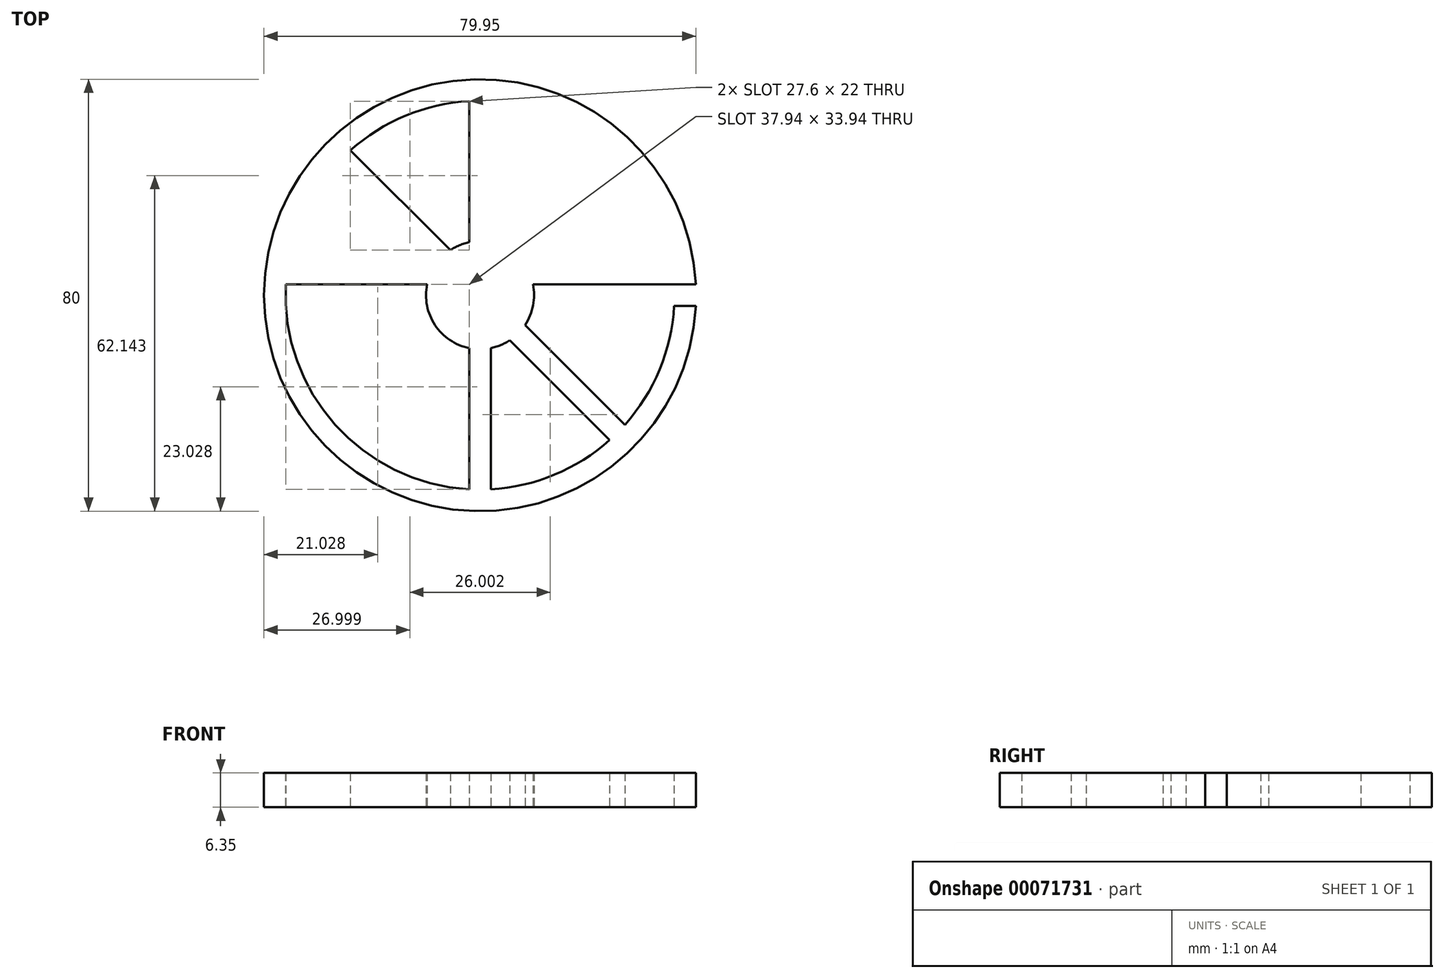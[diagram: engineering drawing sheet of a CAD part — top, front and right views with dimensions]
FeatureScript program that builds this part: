
annotation { "Feature Type Name" : "Feature", "Feature Type Description" : "" }
export const myFeature = defineFeature(function(context is Context, id is Id, definition is map)
    precondition{}
    {
        {
            var Q0;
            Q0=qCreatedBy(makeId("Top.planeOp"),FACE);
            var sketch = newSketch(context, id + "F0", { "sketchPlane" : qUnion([Q0])});
            skCircle(sketch, "E0", {"center": v(0, 0) * mm, "radius": 40 * mm});
            skCircle(sketch, "E1", {"center": v(0, 0) * mm, "radius": 36 * mm});
            skLineSegment(sketch, "E2.bottom", {"start": v(-2, 40) * mm, "end": v(2, 40) * mm});
            skLineSegment(sketch, "E2.top", {"start": v(-2, -40) * mm, "end": v(2, -40) * mm});
            skLineSegment(sketch, "E2.left", {"start": v(-2, 40) * mm, "end": v(-2, -40) * mm});
            skLineSegment(sketch, "E2.right", {"start": v(2, 40) * mm, "end": v(2, -40) * mm});
            skLineSegment(sketch, "E3", {"start": v(2, 0) * mm, "end": v(-2, 0) * mm, "construction": true});
            skPoint(sketch, "E3.endSnap0", {"position": v(-2, 0) * mm});
            skLineSegment(sketch, "E4.bottom", {"start": v(-40, -2) * mm, "end": v(40, -2) * mm});
            skLineSegment(sketch, "E4.top", {"start": v(-40, 2) * mm, "end": v(40, 2) * mm});
            skLineSegment(sketch, "E4.left", {"start": v(-40, 2) * mm, "end": v(-40, -2) * mm});
            skLineSegment(sketch, "E4.right", {"start": v(40, 2) * mm, "end": v(40, -2) * mm});
            skLineSegment(sketch, "E5", {"start": v(0, 2) * mm, "end": v(0, -2) * mm, "construction": true});
            skLineSegment(sketch, "E6.bottom", {"start": v(-26.87, -29.7) * mm, "end": v(29.7, 26.87) * mm});
            skLineSegment(sketch, "E6.top", {"start": v(-29.7, -26.87) * mm, "end": v(26.87, 29.7) * mm});
            skLineSegment(sketch, "E6.left", {"start": v(-29.7, -26.87) * mm, "end": v(-26.87, -29.7) * mm});
            skLineSegment(sketch, "E6.right", {"start": v(26.87, 29.7) * mm, "end": v(29.7, 26.87) * mm});
            skLineSegment(sketch, "E7", {"start": v(-1.41, 1.41) * mm, "end": v(1.41, -1.41) * mm, "construction": true});
            skLineSegment(sketch, "E8.bottom", {"start": v(-29.7, 26.87) * mm, "end": v(-26.87, 29.7) * mm});
            skLineSegment(sketch, "E8.top", {"start": v(26.87, -29.7) * mm, "end": v(29.7, -26.87) * mm});
            skLineSegment(sketch, "E8.left", {"start": v(-29.7, 26.87) * mm, "end": v(26.87, -29.7) * mm});
            skLineSegment(sketch, "E8.right", {"start": v(-26.87, 29.7) * mm, "end": v(29.7, -26.87) * mm});
            skLineSegment(sketch, "E9", {"start": v(-1.41, -1.41) * mm, "end": v(1.41, 1.41) * mm, "construction": true});
            skCircle(sketch, "E10", {"center": v(0, 0) * mm, "radius": 10 * mm});
            skSolve(sketch);
        }
        {
            var Q0;
            {var subQ0=sQuery(id+"F0.wireOp",EDGE,"E2.left");var subQ1=sQuery(id+"F0.wireOp",EDGE,"E0");var subQ2=makeQuery(id+"F0.imprint","INTERSECT",VERTEX,{"disambiguationData":[OD(0.0)],"derivedFrom":[subQ1,subQ0]});Q0=makeQuery(id+"F0.imprint","IMPRINT",FACE,{"disambiguationData":[TD([[makeQuery(id+"F0.imprint","IMPRINT",EDGE,{"disambiguationData":[TD([[subQ2,-1.0]])],"derivedFrom":subQ1}),1.0]])]});}
            var Q1;
            {var subQ1=sQuery(id+"F0.wireOp",EDGE,"E0");var subQ5=sQuery(id+"F0.wireOp",EDGE,"E2.right");var subQ7=makeQuery(id+"F0.imprint","INTERSECT",VERTEX,{"disambiguationData":[OD(0.0)],"derivedFrom":[subQ1,subQ5]});Q1=makeQuery(id+"F0.imprint","IMPRINT",FACE,{"disambiguationData":[TD([[makeQuery(id+"F0.imprint","IMPRINT",EDGE,{"disambiguationData":[TD([[subQ7,-1.0]])],"derivedFrom":subQ1}),1.0]])]});}
            var Q2;
            {var subQ0=sQuery(id+"F0.wireOp",EDGE,"E6.top");var subQ1=sQuery(id+"F0.wireOp",EDGE,"E0");var subQ2=makeQuery(id+"F0.imprint","INTERSECT",VERTEX,{"disambiguationData":[OD(0.0)],"derivedFrom":[subQ1,subQ0]});Q2=makeQuery(id+"F0.imprint","IMPRINT",FACE,{"disambiguationData":[TD([[makeQuery(id+"F0.imprint","IMPRINT",EDGE,{"disambiguationData":[TD([[subQ2,-1.0]])],"derivedFrom":subQ1}),1.0]])]});}
            var Q3;
            {var subQ0=sQuery(id+"F0.wireOp",EDGE,"E6.bottom");var subQ1=sQuery(id+"F0.wireOp",EDGE,"E0");var subQ2=makeQuery(id+"F0.imprint","INTERSECT",VERTEX,{"disambiguationData":[OD(0.0)],"derivedFrom":[subQ1,subQ0]});Q3=makeQuery(id+"F0.imprint","IMPRINT",FACE,{"disambiguationData":[TD([[makeQuery(id+"F0.imprint","IMPRINT",EDGE,{"disambiguationData":[TD([[subQ2,-1.0]])],"derivedFrom":subQ1}),1.0]])]});}
            var Q4;
            {var subQ0=sQuery(id+"F0.wireOp",EDGE,"E4.top");var subQ1=sQuery(id+"F0.wireOp",EDGE,"E0");var subQ2=makeQuery(id+"F0.imprint","INTERSECT",VERTEX,{"disambiguationData":[OD(0.0)],"derivedFrom":[subQ1,subQ0]});Q4=makeQuery(id+"F0.imprint","IMPRINT",FACE,{"disambiguationData":[TD([[makeQuery(id+"F0.imprint","IMPRINT",EDGE,{"disambiguationData":[TD([[subQ2,-1.0]])],"derivedFrom":subQ1}),1.0]])]});}
            var Q5;
            {var subQ1=sQuery(id+"F0.wireOp",EDGE,"E0");var subQ5=sQuery(id+"F0.wireOp",EDGE,"E4.top");var subQ7=makeQuery(id+"F0.imprint","INTERSECT",VERTEX,{"disambiguationData":[OD(0.0)],"derivedFrom":[subQ1,subQ5]});Q5=makeQuery(id+"F0.imprint","IMPRINT",FACE,{"disambiguationData":[TD([[makeQuery(id+"F0.imprint","IMPRINT",EDGE,{"disambiguationData":[TD([[subQ7,1.0]])],"derivedFrom":subQ1}),1.0]])]});}
            var Q6;
            {var subQ0=sQuery(id+"F0.wireOp",EDGE,"E8.right");var subQ1=sQuery(id+"F0.wireOp",EDGE,"E0");var subQ2=makeQuery(id+"F0.imprint","INTERSECT",VERTEX,{"disambiguationData":[OD(1.0)],"derivedFrom":[subQ1,subQ0]});Q6=makeQuery(id+"F0.imprint","IMPRINT",FACE,{"disambiguationData":[TD([[makeQuery(id+"F0.imprint","IMPRINT",EDGE,{"disambiguationData":[TD([[subQ2,-1.0]])],"derivedFrom":subQ1}),1.0]])]});}
            var Q7;
            {var subQ0=sQuery(id+"F0.wireOp",EDGE,"E8.left");var subQ1=sQuery(id+"F0.wireOp",EDGE,"E0");var subQ2=makeQuery(id+"F0.imprint","INTERSECT",VERTEX,{"disambiguationData":[OD(1.0)],"derivedFrom":[subQ1,subQ0]});Q7=makeQuery(id+"F0.imprint","IMPRINT",FACE,{"disambiguationData":[TD([[makeQuery(id+"F0.imprint","IMPRINT",EDGE,{"disambiguationData":[TD([[subQ2,-1.0]])],"derivedFrom":subQ1}),1.0]])]});}
            var Q8;
            {var subQ0=sQuery(id+"F0.wireOp",EDGE,"E2.right");var subQ1=sQuery(id+"F0.wireOp",EDGE,"E0");var subQ2=makeQuery(id+"F0.imprint","INTERSECT",VERTEX,{"disambiguationData":[OD(1.0)],"derivedFrom":[subQ1,subQ0]});Q8=makeQuery(id+"F0.imprint","IMPRINT",FACE,{"disambiguationData":[TD([[makeQuery(id+"F0.imprint","IMPRINT",EDGE,{"disambiguationData":[TD([[subQ2,-1.0]])],"derivedFrom":subQ1}),1.0]])]});}
            var Q9;
            {var subQ0=sQuery(id+"F0.wireOp",EDGE,"E2.left");var subQ5=sQuery(id+"F0.wireOp",EDGE,"E0");var subQ6=makeQuery(id+"F0.imprint","INTERSECT",VERTEX,{"disambiguationData":[OD(1.0)],"derivedFrom":[subQ5,subQ0]});Q9=makeQuery(id+"F0.imprint","IMPRINT",FACE,{"disambiguationData":[TD([[makeQuery(id+"F0.imprint","IMPRINT",EDGE,{"disambiguationData":[TD([[subQ6,-1.0]])],"derivedFrom":subQ5}),1.0]])]});}
            var Q10;
            {var subQ0=sQuery(id+"F0.wireOp",EDGE,"E6.bottom");var subQ1=sQuery(id+"F0.wireOp",EDGE,"E0");var subQ2=makeQuery(id+"F0.imprint","INTERSECT",VERTEX,{"disambiguationData":[OD(1.0)],"derivedFrom":[subQ1,subQ0]});Q10=makeQuery(id+"F0.imprint","IMPRINT",FACE,{"disambiguationData":[TD([[makeQuery(id+"F0.imprint","IMPRINT",EDGE,{"disambiguationData":[TD([[subQ2,-1.0]])],"derivedFrom":subQ1}),1.0]])]});}
            var Q11;
            {var subQ1=sQuery(id+"F0.wireOp",EDGE,"E0");var subQ5=sQuery(id+"F0.wireOp",EDGE,"E6.top");var subQ6=makeQuery(id+"F0.imprint","INTERSECT",VERTEX,{"disambiguationData":[OD(1.0)],"derivedFrom":[subQ1,subQ5]});Q11=makeQuery(id+"F0.imprint","IMPRINT",FACE,{"disambiguationData":[TD([[makeQuery(id+"F0.imprint","IMPRINT",EDGE,{"disambiguationData":[TD([[subQ6,-1.0]])],"derivedFrom":subQ1}),1.0]])]});}
            var Q12;
            {var subQ0=sQuery(id+"F0.wireOp",EDGE,"E4.bottom");var subQ1=sQuery(id+"F0.wireOp",EDGE,"E0");var subQ2=makeQuery(id+"F0.imprint","INTERSECT",VERTEX,{"disambiguationData":[OD(0.0)],"derivedFrom":[subQ1,subQ0]});Q12=makeQuery(id+"F0.imprint","IMPRINT",FACE,{"disambiguationData":[TD([[makeQuery(id+"F0.imprint","IMPRINT",EDGE,{"disambiguationData":[TD([[subQ2,-1.0]])],"derivedFrom":subQ1}),1.0]])]});}
            var Q13;
            {var subQ1=sQuery(id+"F0.wireOp",EDGE,"E0");var subQ5=sQuery(id+"F0.wireOp",EDGE,"E4.top");var subQ8=makeQuery(id+"F0.imprint","INTERSECT",VERTEX,{"disambiguationData":[OD(1.0)],"derivedFrom":[subQ1,subQ5]});Q13=makeQuery(id+"F0.imprint","IMPRINT",FACE,{"disambiguationData":[TD([[makeQuery(id+"F0.imprint","IMPRINT",EDGE,{"disambiguationData":[TD([[subQ8,-1.0]])],"derivedFrom":subQ1}),1.0]])]});}
            var Q14;
            {var subQ0=sQuery(id+"F0.wireOp",EDGE,"E8.left");var subQ1=sQuery(id+"F0.wireOp",EDGE,"E0");var subQ2=makeQuery(id+"F0.imprint","INTERSECT",VERTEX,{"disambiguationData":[OD(0.0)],"derivedFrom":[subQ1,subQ0]});Q14=makeQuery(id+"F0.imprint","IMPRINT",FACE,{"disambiguationData":[TD([[makeQuery(id+"F0.imprint","IMPRINT",EDGE,{"disambiguationData":[TD([[subQ2,-1.0]])],"derivedFrom":subQ1}),1.0]])]});}
            var Q15;
            {var subQ1=sQuery(id+"F0.wireOp",EDGE,"E0");var subQ5=sQuery(id+"F0.wireOp",EDGE,"E8.right");var subQ6=makeQuery(id+"F0.imprint","INTERSECT",VERTEX,{"disambiguationData":[OD(0.0)],"derivedFrom":[subQ1,subQ5]});Q15=makeQuery(id+"F0.imprint","IMPRINT",FACE,{"disambiguationData":[TD([[makeQuery(id+"F0.imprint","IMPRINT",EDGE,{"disambiguationData":[TD([[subQ6,-1.0]])],"derivedFrom":subQ1}),1.0]])]});}
            var Q16;
            {var subQ0=sQuery(id+"F0.wireOp",EDGE,"E2.right");var subQ1=sQuery(id+"F0.wireOp",EDGE,"E1");var subQ2=makeQuery(id+"F0.imprint","INTERSECT",VERTEX,{"disambiguationData":[OD(0.0)],"derivedFrom":[subQ1,subQ0]});Q16=makeQuery(id+"F0.imprint","IMPRINT",FACE,{"disambiguationData":[TD([[makeQuery(id+"F0.imprint","IMPRINT",EDGE,{"disambiguationData":[TD([[subQ2,-1.0]])],"derivedFrom":subQ1}),1.0]])]});}
            var Q17;
            {var subQ0=sQuery(id+"F0.wireOp",EDGE,"E6.bottom");var subQ1=sQuery(id+"F0.wireOp",EDGE,"E1");var subQ2=makeQuery(id+"F0.imprint","INTERSECT",VERTEX,{"disambiguationData":[OD(0.0)],"derivedFrom":[subQ1,subQ0]});Q17=makeQuery(id+"F0.imprint","IMPRINT",FACE,{"disambiguationData":[TD([[makeQuery(id+"F0.imprint","IMPRINT",EDGE,{"disambiguationData":[TD([[subQ2,-1.0]])],"derivedFrom":subQ1}),1.0]])]});}
            var Q18;
            {var subQ0=sQuery(id+"F0.wireOp",EDGE,"E4.top");var subQ1=sQuery(id+"F0.wireOp",EDGE,"E1");var subQ2=makeQuery(id+"F0.imprint","INTERSECT",VERTEX,{"disambiguationData":[OD(0.0)],"derivedFrom":[subQ1,subQ0]});Q18=makeQuery(id+"F0.imprint","IMPRINT",FACE,{"disambiguationData":[TD([[makeQuery(id+"F0.imprint","IMPRINT",EDGE,{"disambiguationData":[TD([[subQ2,1.0]])],"derivedFrom":subQ1}),1.0]])]});}
            var Q19;
            {var subQ0=sQuery(id+"F0.wireOp",EDGE,"E8.right");var subQ1=sQuery(id+"F0.wireOp",EDGE,"E1");var subQ2=makeQuery(id+"F0.imprint","INTERSECT",VERTEX,{"disambiguationData":[OD(0.0)],"derivedFrom":[subQ1,subQ0]});Q19=makeQuery(id+"F0.imprint","IMPRINT",FACE,{"disambiguationData":[TD([[makeQuery(id+"F0.imprint","IMPRINT",EDGE,{"disambiguationData":[TD([[subQ2,-1.0]])],"derivedFrom":subQ1}),1.0]])]});}
            var Q20;
            {var subQ0=sQuery(id+"F0.wireOp",EDGE,"E4.top");var subQ1=sQuery(id+"F0.wireOp",EDGE,"E1");var subQ2=makeQuery(id+"F0.imprint","INTERSECT",VERTEX,{"disambiguationData":[OD(1.0)],"derivedFrom":[subQ1,subQ0]});Q20=makeQuery(id+"F0.imprint","IMPRINT",FACE,{"disambiguationData":[TD([[makeQuery(id+"F0.imprint","IMPRINT",EDGE,{"disambiguationData":[TD([[subQ2,-1.0]])],"derivedFrom":subQ1}),1.0]])]});}
            var Q21;
            {var subQ0=sQuery(id+"F0.wireOp",EDGE,"E6.top");var subQ1=sQuery(id+"F0.wireOp",EDGE,"E1");var subQ2=makeQuery(id+"F0.imprint","INTERSECT",VERTEX,{"disambiguationData":[OD(1.0)],"derivedFrom":[subQ1,subQ0]});Q21=makeQuery(id+"F0.imprint","IMPRINT",FACE,{"disambiguationData":[TD([[makeQuery(id+"F0.imprint","IMPRINT",EDGE,{"disambiguationData":[TD([[subQ2,-1.0]])],"derivedFrom":subQ1}),1.0]])]});}
            var Q22;
            {var subQ0=sQuery(id+"F0.wireOp",EDGE,"E2.left");var subQ1=sQuery(id+"F0.wireOp",EDGE,"E1");var subQ2=makeQuery(id+"F0.imprint","INTERSECT",VERTEX,{"disambiguationData":[OD(1.0)],"derivedFrom":[subQ1,subQ0]});Q22=makeQuery(id+"F0.imprint","IMPRINT",FACE,{"disambiguationData":[TD([[makeQuery(id+"F0.imprint","IMPRINT",EDGE,{"disambiguationData":[TD([[subQ2,-1.0]])],"derivedFrom":subQ1}),1.0]])]});}
            var Q23;
            {var subQ0=sQuery(id+"F0.wireOp",EDGE,"E8.left");var subQ1=sQuery(id+"F0.wireOp",EDGE,"E1");var subQ2=makeQuery(id+"F0.imprint","INTERSECT",VERTEX,{"disambiguationData":[OD(1.0)],"derivedFrom":[subQ1,subQ0]});Q23=makeQuery(id+"F0.imprint","IMPRINT",FACE,{"disambiguationData":[TD([[makeQuery(id+"F0.imprint","IMPRINT",EDGE,{"disambiguationData":[TD([[subQ2,-1.0]])],"derivedFrom":subQ1}),1.0]])]});}
            var Q24;
            {var subQ0=sQuery(id+"F0.wireOp",EDGE,"E8.right");var subQ1=sQuery(id+"F0.wireOp",EDGE,"E4.bottom");var subQ2=makeQuery(id+"F0.imprint","INTERSECT",VERTEX,{"derivedFrom":[subQ1,subQ0]});Q24=makeQuery(id+"F0.imprint","IMPRINT",FACE,{"disambiguationData":[TD([[makeQuery(id+"F0.imprint","IMPRINT",EDGE,{"disambiguationData":[TD([[subQ2,-1.0]])],"derivedFrom":subQ1}),1.0]])]});}
            var Q25;
            {var subQ0=sQuery(id+"F0.wireOp",EDGE,"E6.bottom");var subQ1=sQuery(id+"F0.wireOp",EDGE,"E4.top");var subQ2=makeQuery(id+"F0.imprint","INTERSECT",VERTEX,{"derivedFrom":[subQ1,subQ0]});Q25=makeQuery(id+"F0.imprint","IMPRINT",FACE,{"disambiguationData":[TD([[makeQuery(id+"F0.imprint","IMPRINT",EDGE,{"disambiguationData":[TD([[subQ2,-1.0]])],"derivedFrom":subQ1}),1.0]])]});}
            var Q26;
            {var subQ0=sQuery(id+"F0.wireOp",EDGE,"E6.top");var subQ1=sQuery(id+"F0.wireOp",EDGE,"E2.right");var subQ2=makeQuery(id+"F0.imprint","INTERSECT",VERTEX,{"derivedFrom":[subQ1,subQ0]});Q26=makeQuery(id+"F0.imprint","IMPRINT",FACE,{"disambiguationData":[TD([[makeQuery(id+"F0.imprint","IMPRINT",EDGE,{"disambiguationData":[TD([[subQ2,-1.0]])],"derivedFrom":subQ1}),1.0]])]});}
            var Q27;
            {var subQ0=sQuery(id+"F0.wireOp",EDGE,"E10");var subQ1=sQuery(id+"F0.wireOp",EDGE,"E2.right");var subQ2=makeQuery(id+"F0.imprint","INTERSECT",VERTEX,{"disambiguationData":[OD(0.0)],"derivedFrom":[subQ1,subQ0]});Q27=makeQuery(id+"F0.imprint","IMPRINT",FACE,{"disambiguationData":[TD([[makeQuery(id+"F0.imprint","IMPRINT",EDGE,{"disambiguationData":[TD([[subQ2,-1.0]])],"derivedFrom":subQ1}),1.0]])]});}
            var Q28;
            {var subQ1=sQuery(id+"F0.wireOp",EDGE,"E2.left");var subQ5=sQuery(id+"F0.wireOp",EDGE,"E10");var subQ9=makeQuery(id+"F0.imprint","INTERSECT",VERTEX,{"disambiguationData":[OD(0.0)],"derivedFrom":[subQ1,subQ5]});Q28=makeQuery(id+"F0.imprint","IMPRINT",FACE,{"disambiguationData":[TD([[makeQuery(id+"F0.imprint","IMPRINT",EDGE,{"disambiguationData":[TD([[subQ9,-1.0]])],"derivedFrom":subQ1}),1.0]])]});}
            var Q29;
            {var subQ0=sQuery(id+"F0.wireOp",EDGE,"E10");var subQ1=sQuery(id+"F0.wireOp",EDGE,"E2.left");var subQ2=makeQuery(id+"F0.imprint","INTERSECT",VERTEX,{"disambiguationData":[OD(0.0)],"derivedFrom":[subQ1,subQ0]});Q29=makeQuery(id+"F0.imprint","IMPRINT",FACE,{"disambiguationData":[TD([[makeQuery(id+"F0.imprint","IMPRINT",EDGE,{"disambiguationData":[TD([[subQ2,-1.0]])],"derivedFrom":subQ1}),-1.0]])]});}
            var Q30;
            {var subQ5=sQuery(id+"F0.wireOp",EDGE,"E8.right");var subQ6=sQuery(id+"F0.wireOp",EDGE,"E2.left");var subQ7=makeQuery(id+"F0.imprint","INTERSECT",VERTEX,{"derivedFrom":[subQ6,subQ5]});Q30=makeQuery(id+"F0.imprint","IMPRINT",FACE,{"disambiguationData":[TD([[makeQuery(id+"F0.imprint","IMPRINT",EDGE,{"disambiguationData":[TD([[subQ7,-1.0]])],"derivedFrom":subQ6}),-1.0]])]});}
            var Q31;
            {var subQ0=sQuery(id+"F0.wireOp",EDGE,"E8.left");var subQ1=sQuery(id+"F0.wireOp",EDGE,"E2.right");var subQ2=makeQuery(id+"F0.imprint","INTERSECT",VERTEX,{"derivedFrom":[subQ1,subQ0]});Q31=makeQuery(id+"F0.imprint","IMPRINT",FACE,{"disambiguationData":[TD([[makeQuery(id+"F0.imprint","IMPRINT",EDGE,{"disambiguationData":[TD([[subQ2,-1.0]])],"derivedFrom":subQ1}),1.0]])]});}
            var Q32;
            {var subQ1=sQuery(id+"F0.wireOp",EDGE,"E4.bottom");var subQ6=sQuery(id+"F0.wireOp",EDGE,"E2.right");var subQ9=makeQuery(id+"F0.imprint","INTERSECT",VERTEX,{"derivedFrom":[subQ6,subQ1]});Q32=makeQuery(id+"F0.imprint","IMPRINT",FACE,{"disambiguationData":[TD([[makeQuery(id+"F0.imprint","IMPRINT",EDGE,{"disambiguationData":[TD([[subQ9,-1.0]])],"derivedFrom":subQ6}),1.0]])]});}
            var Q33;
            {var subQ0=sQuery(id+"F0.wireOp",EDGE,"E8.right");var subQ1=sQuery(id+"F0.wireOp",EDGE,"E4.bottom");var subQ2=makeQuery(id+"F0.imprint","INTERSECT",VERTEX,{"derivedFrom":[subQ1,subQ0]});Q33=makeQuery(id+"F0.imprint","IMPRINT",FACE,{"disambiguationData":[TD([[makeQuery(id+"F0.imprint","IMPRINT",EDGE,{"disambiguationData":[TD([[subQ2,-1.0]])],"derivedFrom":subQ1}),-1.0]])]});}
            var Q34;
            {var subQ0=sQuery(id+"F0.wireOp",EDGE,"E6.bottom");var subQ1=sQuery(id+"F0.wireOp",EDGE,"E2.right");var subQ2=makeQuery(id+"F0.imprint","INTERSECT",VERTEX,{"derivedFrom":[subQ1,subQ0]});Q34=makeQuery(id+"F0.imprint","IMPRINT",FACE,{"disambiguationData":[TD([[makeQuery(id+"F0.imprint","IMPRINT",EDGE,{"disambiguationData":[TD([[subQ2,-1.0]])],"derivedFrom":subQ1}),1.0]])]});}
            var Q35;
            {var subQ0=sQuery(id+"F0.wireOp",EDGE,"E4.bottom");var subQ1=sQuery(id+"F0.wireOp",EDGE,"E2.right");var subQ2=makeQuery(id+"F0.imprint","INTERSECT",VERTEX,{"derivedFrom":[subQ1,subQ0]});Q35=makeQuery(id+"F0.imprint","IMPRINT",FACE,{"disambiguationData":[TD([[makeQuery(id+"F0.imprint","IMPRINT",EDGE,{"disambiguationData":[TD([[subQ2,-1.0]])],"derivedFrom":subQ1}),-1.0]])]});}
            var Q36;
            {var subQ0=sQuery(id+"F0.wireOp",EDGE,"E6.bottom");var subQ1=sQuery(id+"F0.wireOp",EDGE,"E2.left");var subQ2=makeQuery(id+"F0.imprint","INTERSECT",VERTEX,{"derivedFrom":[subQ1,subQ0]});Q36=makeQuery(id+"F0.imprint","IMPRINT",FACE,{"disambiguationData":[TD([[makeQuery(id+"F0.imprint","IMPRINT",EDGE,{"disambiguationData":[TD([[subQ2,-1.0]])],"derivedFrom":subQ1}),-1.0]])]});}
            var Q37;
            {var subQ3=sQuery(id+"F0.wireOp",EDGE,"E6.bottom");var subQ5=sQuery(id+"F0.wireOp",EDGE,"E2.left");var subQ6=makeQuery(id+"F0.imprint","INTERSECT",VERTEX,{"derivedFrom":[subQ5,subQ3]});Q37=makeQuery(id+"F0.imprint","IMPRINT",FACE,{"disambiguationData":[TD([[makeQuery(id+"F0.imprint","IMPRINT",EDGE,{"disambiguationData":[TD([[subQ6,-1.0]])],"derivedFrom":subQ5}),1.0]])]});}
            var Q38;
            {var subQ1=sQuery(id+"F0.wireOp",EDGE,"E4.bottom");var subQ5=sQuery(id+"F0.wireOp",EDGE,"E2.left");var subQ6=makeQuery(id+"F0.imprint","INTERSECT",VERTEX,{"derivedFrom":[subQ5,subQ1]});Q38=makeQuery(id+"F0.imprint","IMPRINT",FACE,{"disambiguationData":[TD([[makeQuery(id+"F0.imprint","IMPRINT",EDGE,{"disambiguationData":[TD([[subQ6,-1.0]])],"derivedFrom":subQ5}),-1.0]])]});}
            var Q39;
            {var subQ0=sQuery(id+"F0.wireOp",EDGE,"E10");var subQ1=sQuery(id+"F0.wireOp",EDGE,"E4.bottom");var subQ2=makeQuery(id+"F0.imprint","INTERSECT",VERTEX,{"disambiguationData":[OD(0.0)],"derivedFrom":[subQ1,subQ0]});Q39=makeQuery(id+"F0.imprint","IMPRINT",FACE,{"disambiguationData":[TD([[makeQuery(id+"F0.imprint","IMPRINT",EDGE,{"disambiguationData":[TD([[subQ2,-1.0]])],"derivedFrom":subQ1}),-1.0]])]});}
            var Q40;
            {var subQ5=sQuery(id+"F0.wireOp",EDGE,"E4.bottom");var subQ7=sQuery(id+"F0.wireOp",EDGE,"E10");var subQ9=makeQuery(id+"F0.imprint","INTERSECT",VERTEX,{"disambiguationData":[OD(0.0)],"derivedFrom":[subQ5,subQ7]});Q40=makeQuery(id+"F0.imprint","IMPRINT",FACE,{"disambiguationData":[TD([[makeQuery(id+"F0.imprint","IMPRINT",EDGE,{"disambiguationData":[TD([[subQ9,-1.0]])],"derivedFrom":subQ5}),1.0]])]});}
            var Q41;
            {var subQ0=sQuery(id+"F0.wireOp",EDGE,"E10");var subQ1=sQuery(id+"F0.wireOp",EDGE,"E4.top");var subQ2=makeQuery(id+"F0.imprint","INTERSECT",VERTEX,{"disambiguationData":[OD(0.0)],"derivedFrom":[subQ1,subQ0]});Q41=makeQuery(id+"F0.imprint","IMPRINT",FACE,{"disambiguationData":[TD([[makeQuery(id+"F0.imprint","IMPRINT",EDGE,{"disambiguationData":[TD([[subQ2,-1.0]])],"derivedFrom":subQ1}),1.0]])]});}
            var Q42;
            {var subQ0=sQuery(id+"F0.wireOp",EDGE,"E8.left");var subQ1=sQuery(id+"F0.wireOp",EDGE,"E2.left");var subQ2=makeQuery(id+"F0.imprint","INTERSECT",VERTEX,{"derivedFrom":[subQ1,subQ0]});Q42=makeQuery(id+"F0.imprint","IMPRINT",FACE,{"disambiguationData":[TD([[makeQuery(id+"F0.imprint","IMPRINT",EDGE,{"disambiguationData":[TD([[subQ2,-1.0]])],"derivedFrom":subQ1}),-1.0]])]});}
            var Q43;
            {var subQ0=sQuery(id+"F0.wireOp",EDGE,"E4.bottom");var subQ1=sQuery(id+"F0.wireOp",EDGE,"E2.left");var subQ2=makeQuery(id+"F0.imprint","INTERSECT",VERTEX,{"derivedFrom":[subQ1,subQ0]});Q43=makeQuery(id+"F0.imprint","IMPRINT",FACE,{"disambiguationData":[TD([[makeQuery(id+"F0.imprint","IMPRINT",EDGE,{"disambiguationData":[TD([[subQ2,-1.0]])],"derivedFrom":subQ1}),1.0]])]});}
            var Q44;
            {var subQ0=sQuery(id+"F0.wireOp",EDGE,"E8.left");var subQ1=sQuery(id+"F0.wireOp",EDGE,"E4.bottom");var subQ2=makeQuery(id+"F0.imprint","INTERSECT",VERTEX,{"derivedFrom":[subQ1,subQ0]});Q44=makeQuery(id+"F0.imprint","IMPRINT",FACE,{"disambiguationData":[TD([[makeQuery(id+"F0.imprint","IMPRINT",EDGE,{"disambiguationData":[TD([[subQ2,-1.0]])],"derivedFrom":subQ1}),-1.0]])]});}
            var Q45;
            {var subQ0=sQuery(id+"F0.wireOp",EDGE,"E6.bottom");var subQ1=sQuery(id+"F0.wireOp",EDGE,"E2.right");var subQ2=makeQuery(id+"F0.imprint","INTERSECT",VERTEX,{"derivedFrom":[subQ1,subQ0]});Q45=makeQuery(id+"F0.imprint","IMPRINT",FACE,{"disambiguationData":[TD([[makeQuery(id+"F0.imprint","IMPRINT",EDGE,{"disambiguationData":[TD([[subQ2,-1.0]])],"derivedFrom":subQ1}),-1.0]])]});}
            var Q46;
            {var subQ0=sQuery(id+"F0.wireOp",EDGE,"E8.right");var subQ1=sQuery(id+"F0.wireOp",EDGE,"E2.right");var subQ2=makeQuery(id+"F0.imprint","INTERSECT",VERTEX,{"derivedFrom":[subQ1,subQ0]});Q46=makeQuery(id+"F0.imprint","IMPRINT",FACE,{"disambiguationData":[TD([[makeQuery(id+"F0.imprint","IMPRINT",EDGE,{"disambiguationData":[TD([[subQ2,-1.0]])],"derivedFrom":subQ1}),1.0]])]});}
            var Q47;
            {var subQ0=sQuery(id+"F0.wireOp",EDGE,"E4.top");var subQ1=sQuery(id+"F0.wireOp",EDGE,"E2.right");var subQ2=makeQuery(id+"F0.imprint","INTERSECT",VERTEX,{"derivedFrom":[subQ1,subQ0]});Q47=makeQuery(id+"F0.imprint","IMPRINT",FACE,{"disambiguationData":[TD([[makeQuery(id+"F0.imprint","IMPRINT",EDGE,{"disambiguationData":[TD([[subQ2,-1.0]])],"derivedFrom":subQ1}),1.0]])]});}
            var Q48;
            {var subQ0=sQuery(id+"F0.wireOp",EDGE,"E6.top");var subQ1=sQuery(id+"F0.wireOp",EDGE,"E2.right");var subQ2=makeQuery(id+"F0.imprint","INTERSECT",VERTEX,{"derivedFrom":[subQ1,subQ0]});Q48=makeQuery(id+"F0.imprint","IMPRINT",FACE,{"disambiguationData":[TD([[makeQuery(id+"F0.imprint","IMPRINT",EDGE,{"disambiguationData":[TD([[subQ2,-1.0]])],"derivedFrom":subQ1}),-1.0]])]});}
            var Q49;
            {var subQ0=sQuery(id+"F0.wireOp",EDGE,"E4.top");var subQ1=sQuery(id+"F0.wireOp",EDGE,"E2.right");var subQ2=makeQuery(id+"F0.imprint","INTERSECT",VERTEX,{"derivedFrom":[subQ1,subQ0]});Q49=makeQuery(id+"F0.imprint","IMPRINT",FACE,{"disambiguationData":[TD([[makeQuery(id+"F0.imprint","IMPRINT",EDGE,{"disambiguationData":[TD([[subQ2,-1.0]])],"derivedFrom":subQ1}),-1.0]])]});}
            var Q50;
            {var subQ0=sQuery(id+"F0.wireOp",EDGE,"E8.right");var subQ1=sQuery(id+"F0.wireOp",EDGE,"E2.left");var subQ2=makeQuery(id+"F0.imprint","INTERSECT",VERTEX,{"derivedFrom":[subQ1,subQ0]});Q50=makeQuery(id+"F0.imprint","IMPRINT",FACE,{"disambiguationData":[TD([[makeQuery(id+"F0.imprint","IMPRINT",EDGE,{"disambiguationData":[TD([[subQ2,-1.0]])],"derivedFrom":subQ1}),1.0]])]});}
            var Q51;
            {var subQ0=sQuery(id+"F0.wireOp",EDGE,"E6.top");var subQ1=sQuery(id+"F0.wireOp",EDGE,"E4.top");var subQ2=makeQuery(id+"F0.imprint","INTERSECT",VERTEX,{"derivedFrom":[subQ1,subQ0]});Q51=makeQuery(id+"F0.imprint","IMPRINT",FACE,{"disambiguationData":[TD([[makeQuery(id+"F0.imprint","IMPRINT",EDGE,{"disambiguationData":[TD([[subQ2,-1.0]])],"derivedFrom":subQ1}),1.0]])]});}
            var Q52;
            {var subQ0=sQuery(id+"F0.wireOp",EDGE,"E4.top");var subQ1=sQuery(id+"F0.wireOp",EDGE,"E2.left");var subQ2=makeQuery(id+"F0.imprint","INTERSECT",VERTEX,{"derivedFrom":[subQ1,subQ0]});Q52=makeQuery(id+"F0.imprint","IMPRINT",FACE,{"disambiguationData":[TD([[makeQuery(id+"F0.imprint","IMPRINT",EDGE,{"disambiguationData":[TD([[subQ2,-1.0]])],"derivedFrom":subQ1}),-1.0]])]});}
            var Q53;
            {var subQ0=sQuery(id+"F0.wireOp",EDGE,"E6.top");var subQ13=sQuery(id+"F0.wireOp",EDGE,"E2.left");var subQ14=makeQuery(id+"F0.imprint","INTERSECT",VERTEX,{"derivedFrom":[subQ13,subQ0]});Q53=makeQuery(id+"F0.imprint","IMPRINT",FACE,{"disambiguationData":[TD([[makeQuery(id+"F0.imprint","IMPRINT",EDGE,{"disambiguationData":[TD([[subQ14,-1.0]])],"derivedFrom":subQ13}),1.0]])]});}
            var Q54;
            {var subQ0=sQuery(id+"F0.wireOp",EDGE,"E4.top");var subQ1=sQuery(id+"F0.wireOp",EDGE,"E2.left");var subQ2=makeQuery(id+"F0.imprint","INTERSECT",VERTEX,{"derivedFrom":[subQ1,subQ0]});Q54=makeQuery(id+"F0.imprint","IMPRINT",FACE,{"disambiguationData":[TD([[makeQuery(id+"F0.imprint","IMPRINT",EDGE,{"disambiguationData":[TD([[subQ2,-1.0]])],"derivedFrom":subQ1}),1.0]])]});}
            var Q55;
            {var subQ0=sQuery(id+"F0.wireOp",EDGE,"E6.top");var subQ1=sQuery(id+"F0.wireOp",EDGE,"E2.left");var subQ2=makeQuery(id+"F0.imprint","INTERSECT",VERTEX,{"derivedFrom":[subQ1,subQ0]});Q55=makeQuery(id+"F0.imprint","IMPRINT",FACE,{"disambiguationData":[TD([[makeQuery(id+"F0.imprint","IMPRINT",EDGE,{"disambiguationData":[TD([[subQ2,-1.0]])],"derivedFrom":subQ1}),-1.0]])]});}
            var Q56;
            {var subQ0=sQuery(id+"F0.wireOp",EDGE,"E8.left");var subQ1=sQuery(id+"F0.wireOp",EDGE,"E2.left");var subQ2=makeQuery(id+"F0.imprint","INTERSECT",VERTEX,{"derivedFrom":[subQ1,subQ0]});Q56=makeQuery(id+"F0.imprint","IMPRINT",FACE,{"disambiguationData":[TD([[makeQuery(id+"F0.imprint","IMPRINT",EDGE,{"disambiguationData":[TD([[subQ2,-1.0]])],"derivedFrom":subQ1}),1.0]])]});}
            extrude(context, id + "F1", {"entities" : qUnion([Q0, Q1, Q2, Q3, Q4, Q5, Q6, Q7, Q8, Q9, Q10, Q11, Q12, Q13, Q14, Q15, Q16, Q17, Q18, Q19, Q20, Q21, Q22, Q23, Q24, Q25, Q26, Q27, Q28, Q29, Q30, Q31, Q32, Q33, Q34, Q35, Q36, Q37, Q38, Q39, Q40, Q41, Q42, Q43, Q44, Q45, Q46, Q47, Q48, Q49, Q50, Q51, Q52, Q53, Q54, Q55, Q56]), "depth" : 6.35 * mm});
        }
    });
